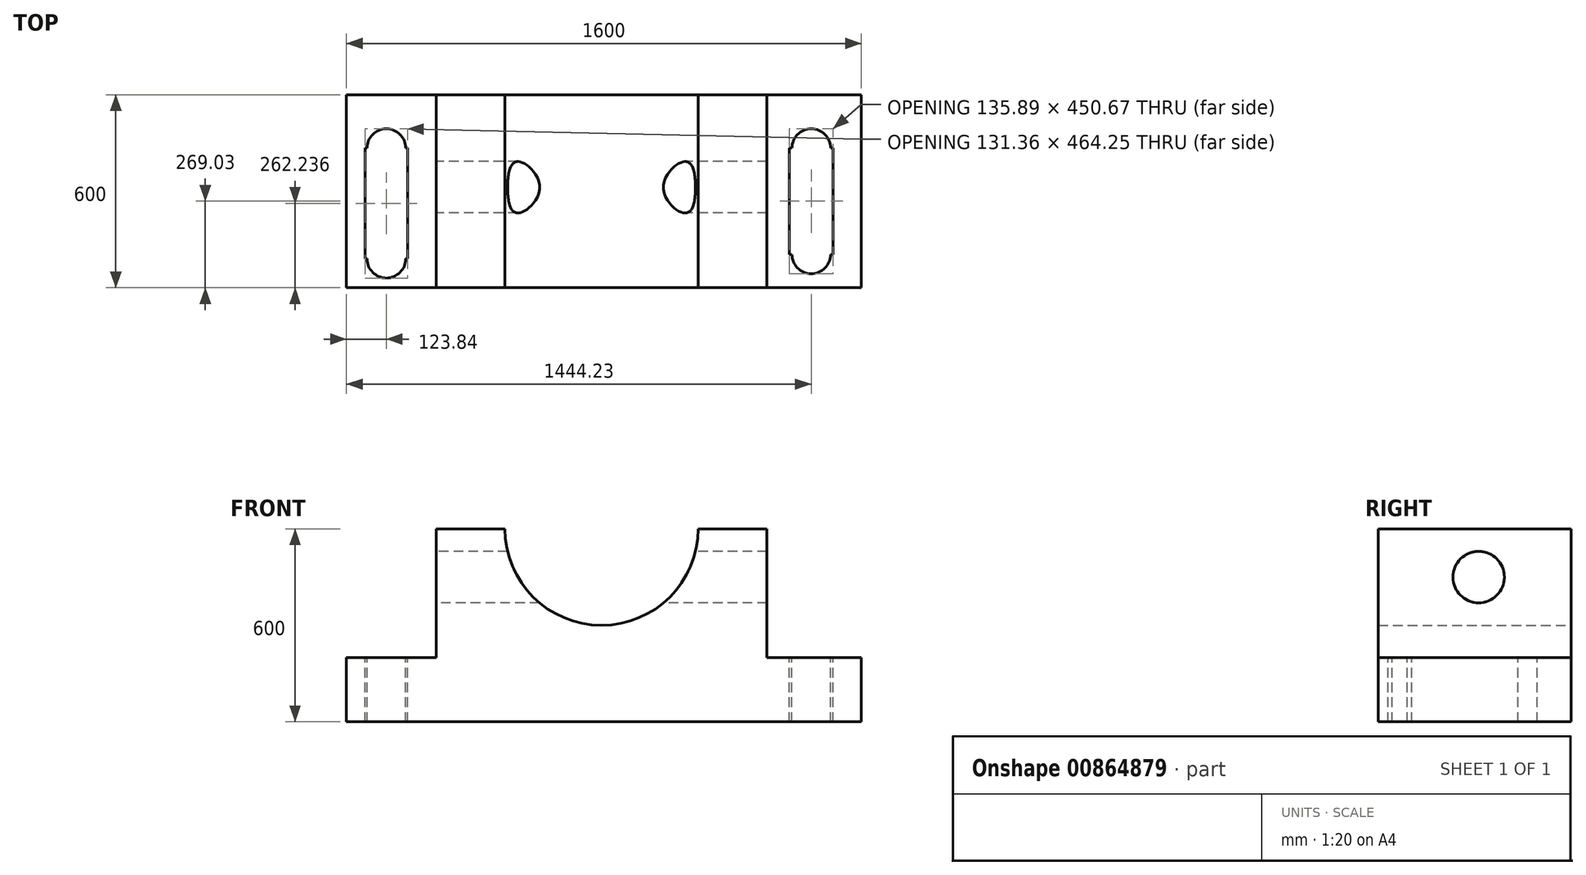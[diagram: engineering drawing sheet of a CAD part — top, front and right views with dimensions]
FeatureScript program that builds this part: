
annotation { "Feature Type Name" : "Feature", "Feature Type Description" : "" }
export const myFeature = defineFeature(function(context is Context, id is Id, definition is map)
    precondition{}
    {
        {
            var Q0;
            Q0=qCreatedBy(makeId("Front.planeOp"),FACE);
            var sketch = newSketch(context, id + "F0", { "sketchPlane" : qUnion([Q0])});
            skLineSegment(sketch, "E0.bottom", {"start": v(506.8, 300) * mm, "end": v(292.53, 300) * mm});
            skLineSegment(sketch, "E0.top", {"start": v(800, -300) * mm, "end": v(-800, -300) * mm});
            skLineSegment(sketch, "E0.left", {"start": v(800, -100) * mm, "end": v(800, -300) * mm});
            skLineSegment(sketch, "E0.right", {"start": v(-800, -100) * mm, "end": v(-800, -300) * mm});
            skPoint(sketch, "E0.middle", {"position": v(0, 0) * mm});
            skLineSegment(sketch, "E1", {"start": v(-521.75, 300) * mm, "end": v(-521.75, -100) * mm});
            skLineSegment(sketch, "E2", {"start": v(-521.75, -100) * mm, "end": v(-800, -100) * mm});
            skLineSegment(sketch, "E3", {"start": v(506.8, 300) * mm, "end": v(506.8, -100) * mm});
            skLineSegment(sketch, "E4", {"start": v(506.8, -100) * mm, "end": v(800, -100) * mm});
            skPoint(sketch, "E5.orphan", {"position": v(-800, 300) * mm});
            skPoint(sketch, "E6.orphan", {"position": v(800, 300) * mm});
            skArc(sketch, "E7", {"start": v(-307.47, 300) * mm, "mid": v(-7.47, 0) * mm, "end": v(292.53, 300) * mm});
            skLineSegment(sketch, "E8.trimOffspring", {"start": v(-307.47, 300) * mm, "end": v(-521.75, 300) * mm});
            skSolve(sketch);
        }
        {
            var Q0;
            Q0 = qSketchRegion(id + "F0", true);
            extrude(context, id + "F1", {"entities" : qUnion([Q0]), "depth" : 600 * mm, "offsetDistance" : 25 * mm});
        }
        {
            var Q0;
            Q0=makeQuery(id+"F1.opExtrude","SWEPT_FACE",FACE,{"disambiguationData":[OSD([sQuery(id+"F0.wireOp",EDGE,"E1")])]});
            var sketch = newSketch(context, id + "F2", { "sketchPlane" : qUnion([Q0])});
            skCircle(sketch, "E9", {"center": v(287.71, 150) * mm, "radius": 80 * mm});
            skSolve(sketch);
        }
        {
            var Q0;
            Q0 = qSketchRegion(id + "F2", true);
            var Q1;
            Q1 = qSketchRegion(id + "FV98aDC2eeBgk2K_1", true);
            extrude(context, id + "F3", {"entities" : qUnion([Q0, Q1]), "operationType" : NewBodyOperationType.REMOVE, "endBound" : BoundingType.THROUGH_ALL, "oppositeDirection" : true, "depth" : 25 * mm, "offsetDistance" : 25 * mm});
        }
        {
            var Q0;
            Q0=makeQuery(id+"F1.opExtrude","SWEPT_FACE",FACE,{"disambiguationData":[OSD([sQuery(id+"F0.wireOp",EDGE,"E4")])]});
            var sketch = newSketch(context, id + "F4", { "sketchPlane" : qUnion([Q0])});
            skLineSegment(sketch, "E10.bottom", {"start": v(-610.48, -165.64) * mm, "end": v(-616.16, -165.64) * mm});
            skLineSegment(sketch, "E10.top", {"start": v(-610.48, -509.9) * mm, "end": v(-616.16, -509.9) * mm});
            skLineSegment(sketch, "E10.left", {"start": v(-610.48, -165.64) * mm, "end": v(-610.48, -509.9) * mm});
            skLineSegment(sketch, "E10.right", {"start": v(-741.84, -165.64) * mm, "end": v(-741.84, -509.9) * mm});
            skPoint(sketch, "E10.middle", {"position": v(-676.16, -337.76) * mm});
            skLineSegment(sketch, "E11.top", {"start": v(712.18, -496.3) * mm, "end": v(704.24, -496.3) * mm});
            skLineSegment(sketch, "E11.left", {"start": v(712.18, -165.64) * mm, "end": v(712.18, -496.3) * mm});
            skLineSegment(sketch, "E11.right", {"start": v(576.3, -165.64) * mm, "end": v(576.3, -496.3) * mm});
            skPoint(sketch, "E11.middle", {"position": v(644.24, -330.97) * mm});
            skArc(sketch, "E12", {"start": v(-616.16, -165.64) * mm, "mid": v(-676.16, -105.64) * mm, "end": v(-736.16, -165.64) * mm});
            skArc(sketch, "E13", {"start": v(-736.16, -509.9) * mm, "mid": v(-676.16, -569.9) * mm, "end": v(-616.16, -509.9) * mm});
            skArc(sketch, "E14", {"start": v(584.24, -496.3) * mm, "mid": v(644.24, -556.3) * mm, "end": v(704.24, -496.3) * mm});
            skLineSegment(sketch, "E15.trimOffspring", {"start": v(-736.16, -165.64) * mm, "end": v(-741.84, -165.64) * mm});
            skLineSegment(sketch, "E16.trimOffspring", {"start": v(-736.16, -509.9) * mm, "end": v(-741.84, -509.9) * mm});
            skPoint(sketch, "E17.trimOffspring.start.orphan", {"position": v(644.24, -165.64) * mm});
            skArc(sketch, "E18", {"start": v(704.24, -165.64) * mm, "mid": v(644.24, -105.64) * mm, "end": v(584.24, -165.64) * mm});
            skLineSegment(sketch, "E19.trimOffspring", {"start": v(584.24, -496.3) * mm, "end": v(576.3, -496.3) * mm});
            skLineSegment(sketch, "E20", {"start": v(712.18, -165.64) * mm, "end": v(704.24, -165.64) * mm});
            skLineSegment(sketch, "E21.trimOffspring", {"start": v(584.24, -165.64) * mm, "end": v(576.3, -165.64) * mm});
            skSolve(sketch);
        }
        {
            var Q0;
            Q0 = qSketchRegion(id + "F4", true);
            extrude(context, id + "F5", {"entities" : qUnion([Q0]), "operationType" : NewBodyOperationType.REMOVE, "endBound" : BoundingType.THROUGH_ALL, "oppositeDirection" : true, "depth" : 25 * mm, "offsetDistance" : 25 * mm});
        }
        {
            var Q0;
            Q0 = qSketchRegion(id + "F4", true);
            extrude(context, id + "F6", {"entities" : qUnion([Q0]), "operationType" : NewBodyOperationType.REMOVE, "endBound" : BoundingType.THROUGH_ALL, "oppositeDirection" : true, "depth" : 25 * mm, "offsetDistance" : 25 * mm});
        }
    });
